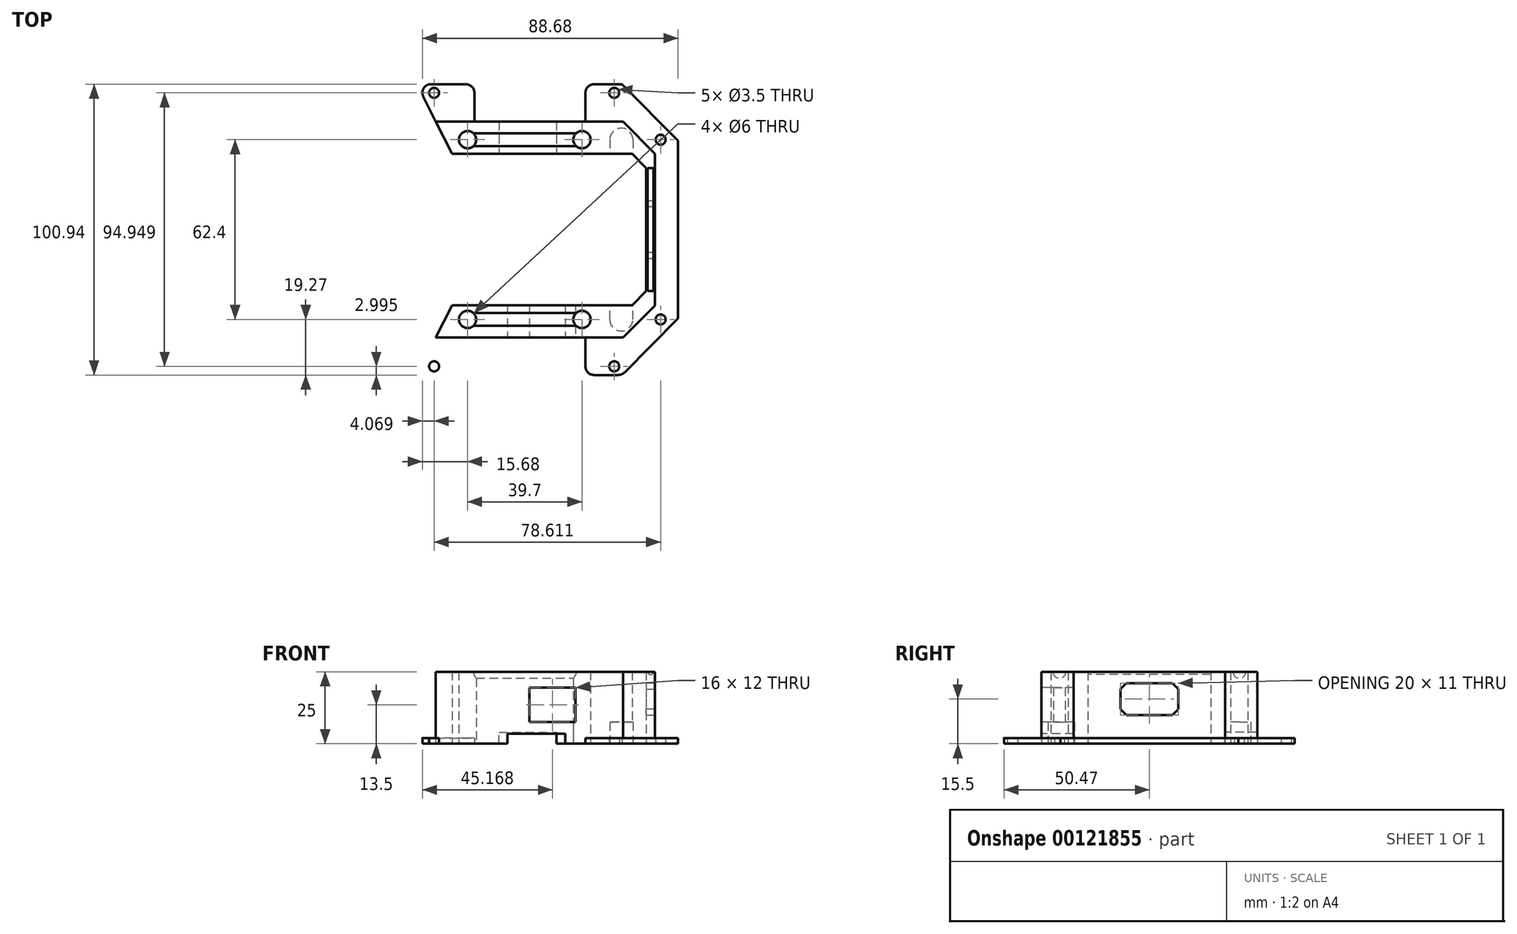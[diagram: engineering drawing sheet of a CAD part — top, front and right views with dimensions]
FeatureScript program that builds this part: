
annotation { "Feature Type Name" : "Feature", "Feature Type Description" : "" }
export const myFeature = defineFeature(function(context is Context, id is Id, definition is map)
    precondition{}
    {
        {
            var Q0;
            Q0=qCreatedBy(makeId("Top.planeOp"),FACE);
            var sketch = newSketch(context, id + "F0", { "sketchPlane" : qUnion([Q0])});
            skCircle(sketch, "E0", {"center": v(-9.61, 47.47) * mm, "radius": 1.75 * mm});
            skCircle(sketch, "E1", {"center": v(52.89, 47.47) * mm, "radius": 1.75 * mm});
            skCircle(sketch, "E2", {"center": v(69, 31.2) * mm, "radius": 1.75 * mm});
            skCircle(sketch, "E3", {"center": v(2, 31.2) * mm, "radius": 3 * mm});
            skLineSegment(sketch, "E4.MirrorCS", {"start": v(55.55, 50.47) * mm, "end": v(-15.54, 50.47) * mm});
            skLineSegment(sketch, "E5.MirrorCS", {"start": v(-9.01, 37.47) * mm, "end": v(55.99, 37.47) * mm});
            skCircle(sketch, "E6", {"center": v(41.7, 31.2) * mm, "radius": 3 * mm});
            skLineSegment(sketch, "E7", {"start": v(-5.97, 31.4) * mm, "end": v(-15.54, 50.47) * mm});
            skLineSegment(sketch, "E8", {"start": v(52.89, 47.47) * mm, "end": v(69, 31.2) * mm, "construction": true});
            skLineSegment(sketch, "E9", {"start": v(55.55, 50.47) * mm, "end": v(75, 30.82) * mm});
            skLineSegment(sketch, "E10", {"start": v(55.99, 37.47) * mm, "end": v(67, 26.35) * mm});
            skLineSegment(sketch, "E11", {"start": v(75, 30.82) * mm, "end": v(75, -30.82) * mm});
            skLineSegment(sketch, "E12", {"start": v(69, 31.2) * mm, "end": v(2, 31.2) * mm, "construction": true});
            skLineSegment(sketch, "E13", {"start": v(65.5, 40.42) * mm, "end": v(62.66, 37.6) * mm, "construction": true});
            skCircle(sketch, "E14.MirrorC", {"center": v(52.89, -47.47) * mm, "radius": 1.75 * mm});
            skCircle(sketch, "E15.MirrorC", {"center": v(69, -31.2) * mm, "radius": 1.75 * mm});
            skLineSegment(sketch, "E16.MirrorCS", {"start": v(62.66, -37.6) * mm, "end": v(58.9, -34.3) * mm, "construction": true});
            skCircle(sketch, "E17.MirrorC", {"center": v(-9.61, -47.47) * mm, "radius": 1.75 * mm});
            skLineSegment(sketch, "E18.MirrorCS", {"start": v(65.5, -40.42) * mm, "end": v(62.66, -37.6) * mm, "construction": true});
            skLineSegment(sketch, "E19.MirrorCS", {"start": v(55.99, -37.47) * mm, "end": v(67, -26.35) * mm});
            skLineSegment(sketch, "E20.MirrorCS", {"start": v(-5.97, -31.4) * mm, "end": v(-15.54, -50.47) * mm});
            skLineSegment(sketch, "E21.MirrorCS", {"start": v(52.89, -47.47) * mm, "end": v(-9.61, -47.47) * mm, "construction": true});
            skCircle(sketch, "E22.MirrorC", {"center": v(41.7, -31.2) * mm, "radius": 3 * mm});
            skLineSegment(sketch, "E23.MirrorCS", {"start": v(-9.01, -37.47) * mm, "end": v(55.99, -37.47) * mm});
            skCircle(sketch, "E24.MirrorC", {"center": v(2, -31.2) * mm, "radius": 3 * mm});
            skLineSegment(sketch, "E25.MirrorCS", {"start": v(55.55, -50.47) * mm, "end": v(75, -30.82) * mm});
            skLineSegment(sketch, "E26.MirrorCS", {"start": v(52.89, -47.47) * mm, "end": v(69, -31.2) * mm, "construction": true});
            skLineSegment(sketch, "E27.MirrorCS", {"start": v(69, -31.2) * mm, "end": v(2, -31.2) * mm, "construction": true});
            skLineSegment(sketch, "E28.MirrorCS", {"start": v(55.55, -50.47) * mm, "end": v(-15.54, -50.47) * mm});
            skLineSegment(sketch, "E29", {"start": v(67, 26.35) * mm, "end": v(67, -26.35) * mm});
            skLineSegment(sketch, "E30", {"start": v(-5.86, 31.2) * mm, "end": v(62.2, 31.2) * mm});
            skLineSegment(sketch, "E31.MirrorCS", {"start": v(-5.86, -31.2) * mm, "end": v(62.2, -31.2) * mm});
            skLineSegment(sketch, "E32", {"start": v(42.89, 50.47) * mm, "end": v(42.89, 37.47) * mm});
            skLineSegment(sketch, "E33", {"start": v(4.39, 50.47) * mm, "end": v(4.39, 37.47) * mm});
            skLineSegment(sketch, "E34.MirrorCS", {"start": v(42.89, -50.47) * mm, "end": v(42.89, -37.47) * mm});
            skLineSegment(sketch, "E35.MirrorCS", {"start": v(4.39, -50.47) * mm, "end": v(4.39, -37.47) * mm});
            skLineSegment(sketch, "E36", {"start": v(54.2, -31.2) * mm, "end": v(64, -21.3) * mm});
            skLineSegment(sketch, "E37.MirrorCS", {"start": v(54.2, 31.2) * mm, "end": v(64, 21.3) * mm});
            skLineSegment(sketch, "E38", {"start": v(64, 21.3) * mm, "end": v(64, -21.3) * mm});
            skLineSegment(sketch, "E39", {"start": v(59.1, 26.25) * mm, "end": v(-3.38, 26.25) * mm});
            skLineSegment(sketch, "E40", {"start": v(-3.38, 26.25) * mm, "end": v(-5.97, 31.4) * mm});
            skLineSegment(sketch, "E41.MirrorCS", {"start": v(59.1, -26.25) * mm, "end": v(-3.38, -26.25) * mm});
            skLineSegment(sketch, "E42.MirrorCS", {"start": v(-3.38, -26.25) * mm, "end": v(-5.97, -31.4) * mm});
            skLineSegment(sketch, "E43", {"start": v(52.89, 47.47) * mm, "end": v(-9.61, 47.47) * mm, "construction": true});
            skSolve(sketch);
        }
        {
            var Q0;
            {var subQ0=sQuery(id+"F0.wireOp",EDGE,"4sFYRNq8-8Jgj-4G77-OglM-QNHqH1h9Sw3j");Q0=makeQuery(id+"F0.imprint","IMPRINT",FACE,{"disambiguationData":[TD([[makeQuery(id+"F0.imprint","IMPRINT",EDGE,{"derivedFrom":subQ0}),-1.0]])]});}
            var Q1;
            {var subQ7=sQuery(id+"F0.wireOp",EDGE,"8FFk7yXp-FnWU-P27a-pTHK-MUgHDnBpdSHA");Q1=makeQuery(id+"F0.imprint","IMPRINT",FACE,{"disambiguationData":[TD([[makeQuery(id+"F0.imprint","IMPRINT",EDGE,{"derivedFrom":subQ7}),-1.0]])]});}
            var Q2;
            Q2=makeQuery(id+"F0.imprint","IMPRINT",FACE,{"disambiguationData":[TD([[makeQuery(id+"F0.imprint","IMPRINT",EDGE,{"derivedFrom":sQuery(id+"F0.wireOp",EDGE,"E0")}),-1.0]])]});
            var Q3;
            Q3=makeQuery(id+"F0.imprint","IMPRINT",FACE,{"disambiguationData":[TD([[makeQuery(id+"F0.imprint","IMPRINT",EDGE,{"derivedFrom":sQuery(id+"F0.wireOp",EDGE,"4ea4419b-eab7-4580-8047-e2baf9f9c4100.MirrorC")}),1.0]])]});
            var Q4;
            Q4=makeQuery(id+"F0.imprint","IMPRINT",FACE,{"disambiguationData":[TD([[makeQuery(id+"F0.imprint","IMPRINT",EDGE,{"derivedFrom":sQuery(id+"F0.wireOp",EDGE,"f24bded4-04d1-417a-8021-171b2d75794f0.MirrorC")}),1.0]])]});
            var Q5;
            {var subQ0=sQuery(id+"F0.wireOp",EDGE,"pAdb5JEh-NYMF-ctJB-lSUV-qMQ0hBkF58aF");var subQ1=sQuery(id+"F0.wireOp",EDGE,"931a9ce9-199b-493e-a000-b7f4cd656f313.MirrorCS");var subQ2=makeQuery(id+"F0.imprint","INTERSECT",VERTEX,{"derivedFrom":[subQ1,subQ0]});Q5=makeQuery(id+"F0.imprint","IMPRINT",FACE,{"disambiguationData":[TD([[makeQuery(id+"F0.imprint","IMPRINT",EDGE,{"disambiguationData":[TD([[subQ2,-1.0]])],"derivedFrom":subQ1}),-1.0]])]});}
            var Q6;
            Q6=makeQuery(id+"F0.imprint","IMPRINT",FACE,{"disambiguationData":[TD([[makeQuery(id+"F0.imprint","IMPRINT",EDGE,{"derivedFrom":sQuery(id+"F0.wireOp",EDGE,"f24bded4-04d1-417a-8021-171b2d75794f1.MirrorC")}),1.0]])]});
            var Q7;
            Q7=makeQuery(id+"F0.imprint","IMPRINT",FACE,{"disambiguationData":[TD([[makeQuery(id+"F0.imprint","IMPRINT",EDGE,{"derivedFrom":sQuery(id+"F0.wireOp",EDGE,"E1")}),-1.0]])]});
            var Q8;
            Q8=makeQuery(id+"F0.imprint","IMPRINT",FACE,{"disambiguationData":[TD([[makeQuery(id+"F0.imprint","IMPRINT",EDGE,{"derivedFrom":sQuery(id+"F0.wireOp",EDGE,"E17.MirrorC")}),1.0]])]});
            extrude(context, id + "F1", {"entities" : qUnion([Q0, Q1, Q2, Q3, Q4, Q5, Q6, Q7, Q8]), "depth" : 2 * mm, "offsetDistance" : 25 * mm});
        }
        {
            var Q0;
            {var subQ1=sQuery(id+"F0.wireOp",EDGE,"a8754a4c-98fa-47e2-aac1-e6e8d69fb4766.MirrorCS");var subQ3=sQuery(id+"F0.wireOp",EDGE,"a8754a4c-98fa-47e2-aac1-e6e8d69fb4767.MirrorCS");var subQ4=makeQuery(id+"F0.imprint","INTERSECT",VERTEX,{"derivedFrom":[subQ1,subQ3]});Q0=makeQuery(id+"F0.imprint","IMPRINT",FACE,{"disambiguationData":[TD([[makeQuery(id+"F0.imprint","IMPRINT",EDGE,{"disambiguationData":[TD([[subQ4,1.0]])],"derivedFrom":subQ3}),-1.0]])]});}
            var Q1;
            {var subQ7=sQuery(id+"F0.wireOp",EDGE,"a8754a4c-98fa-47e2-aac1-e6e8d69fb4764.MirrorCS");Q1=makeQuery(id+"F0.imprint","IMPRINT",FACE,{"disambiguationData":[TD([[makeQuery(id+"F0.imprint","IMPRINT",EDGE,{"derivedFrom":subQ7}),1.0]])]});}
            var Q2;
            {var subQ6=sQuery(id+"F0.wireOp",EDGE,"E5.MirrorCS");Q2=makeQuery(id+"F0.imprint","IMPRINT",FACE,{"disambiguationData":[TD([[makeQuery(id+"F0.imprint","IMPRINT",EDGE,{"derivedFrom":subQ6}),-1.0]])]});}
            var Q3;
            {var subQ1=sQuery(id+"F0.wireOp",EDGE,"dWmuS8xV-OHKk-HRkj-rr6b-XV2wZqhuztuN");Q3=makeQuery(id+"F0.imprint","IMPRINT",FACE,{"disambiguationData":[TD([[makeQuery(id+"F0.imprint","IMPRINT",EDGE,{"derivedFrom":subQ1}),1.0]])]});}
            var Q4;
            {var subQ8=sQuery(id+"F0.wireOp",EDGE,"4ea4419b-eab7-4580-8047-e2baf9f9c4108.MirrorCS");Q4=makeQuery(id+"F0.imprint","IMPRINT",FACE,{"disambiguationData":[TD([[makeQuery(id+"F0.imprint","IMPRINT",EDGE,{"derivedFrom":subQ8}),1.0]])]});}
            var Q5;
            {var subQ1=sQuery(id+"F0.wireOp",EDGE,"4ea4419b-eab7-4580-8047-e2baf9f9c4102.MirrorCS");var subQ3=sQuery(id+"F0.wireOp",EDGE,"4ea4419b-eab7-4580-8047-e2baf9f9c4103.MirrorCS");var subQ4=makeQuery(id+"F0.imprint","INTERSECT",VERTEX,{"derivedFrom":[subQ1,subQ3]});Q5=makeQuery(id+"F0.imprint","IMPRINT",FACE,{"disambiguationData":[TD([[makeQuery(id+"F0.imprint","IMPRINT",EDGE,{"disambiguationData":[TD([[subQ4,-1.0]])],"derivedFrom":subQ3}),-1.0]])]});}
            var Q6;
            {var subQ5=sQuery(id+"F0.wireOp",EDGE,"pAdb5JEh-NYMF-ctJB-lSUV-qMQ0hBkF58aF");Q6=makeQuery(id+"F0.imprint","IMPRINT",FACE,{"disambiguationData":[TD([[makeQuery(id+"F0.imprint","IMPRINT",EDGE,{"derivedFrom":subQ5}),-1.0]])]});}
            var Q7;
            {var subQ0=sQuery(id+"F0.wireOp",EDGE,"4ea4419b-eab7-4580-8047-e2baf9f9c4105.MirrorCS");var subQ1=sQuery(id+"F0.wireOp",EDGE,"4ea4419b-eab7-4580-8047-e2baf9f9c4103.MirrorCS");var subQ2=makeQuery(id+"F0.imprint","INTERSECT",VERTEX,{"derivedFrom":[subQ1,subQ0]});Q7=makeQuery(id+"F0.imprint","IMPRINT",FACE,{"disambiguationData":[TD([[makeQuery(id+"F0.imprint","IMPRINT",EDGE,{"disambiguationData":[TD([[subQ2,-1.0]])],"derivedFrom":subQ1}),-1.0]])]});}
            var Q8;
            {var subQ5=sQuery(id+"F0.wireOp",EDGE,"f24bded4-04d1-417a-8021-171b2d75794f8.MirrorCS");Q8=makeQuery(id+"F0.imprint","IMPRINT",FACE,{"disambiguationData":[TD([[makeQuery(id+"F0.imprint","IMPRINT",EDGE,{"derivedFrom":subQ5}),1.0]])]});}
            var Q9;
            {var subQ0=sQuery(id+"F0.wireOp",EDGE,"f24bded4-04d1-417a-8021-171b2d75794f7.MirrorCS");Q9=makeQuery(id+"F0.imprint","IMPRINT",FACE,{"disambiguationData":[TD([[makeQuery(id+"F0.imprint","IMPRINT",EDGE,{"derivedFrom":subQ0}),1.0]])]});}
            var Q10;
            {var subQ5=sQuery(id+"F0.wireOp",EDGE,"a31a7e4d-a42e-4eae-b5b2-72da23cc9b960.MirrorCS");Q10=makeQuery(id+"F0.imprint","IMPRINT",FACE,{"disambiguationData":[TD([[makeQuery(id+"F0.imprint","IMPRINT",EDGE,{"derivedFrom":subQ5}),-1.0]])]});}
            var Q11;
            {var subQ4=sQuery(id+"F0.wireOp",EDGE,"4ea4419b-eab7-4580-8047-e2baf9f9c41013.MirrorCS");var subQ6=sQuery(id+"F0.wireOp",EDGE,"pAdb5JEh-NYMF-ctJB-lSUV-qMQ0hBkF58aF");var subQ7=makeQuery(id+"F0.imprint","INTERSECT",VERTEX,{"derivedFrom":[subQ6,subQ4]});Q11=makeQuery(id+"F0.imprint","IMPRINT",FACE,{"disambiguationData":[TD([[makeQuery(id+"F0.imprint","IMPRINT",EDGE,{"disambiguationData":[TD([[subQ7,1.0]])],"derivedFrom":subQ6}),-1.0]])]});}
            var Q12;
            {var subQ0=sQuery(id+"F0.wireOp",EDGE,"E23.MirrorCS");var subQ9=sQuery(id+"F0.wireOp",EDGE,"E19.MirrorCS");var subQ10=makeQuery(id+"F0.imprint","INTERSECT",VERTEX,{"derivedFrom":[subQ9,subQ0]});Q12=makeQuery(id+"F0.imprint","IMPRINT",FACE,{"disambiguationData":[TD([[makeQuery(id+"F0.imprint","IMPRINT",EDGE,{"disambiguationData":[TD([[subQ10,-1.0]])],"derivedFrom":subQ9}),1.0]])]});}
            var Q13;
            {var subQ4=sQuery(id+"F0.wireOp",EDGE,"E29");Q13=makeQuery(id+"F0.imprint","IMPRINT",FACE,{"disambiguationData":[TD([[makeQuery(id+"F0.imprint","IMPRINT",EDGE,{"derivedFrom":subQ4}),-1.0]])]});}
            var Q14;
            {var subQ10=sQuery(id+"F0.wireOp",EDGE,"E39");Q14=makeQuery(id+"F0.imprint","IMPRINT",FACE,{"disambiguationData":[TD([[makeQuery(id+"F0.imprint","IMPRINT",EDGE,{"derivedFrom":subQ10}),-1.0]])]});}
            var Q15;
            {var subQ9=sQuery(id+"F0.wireOp",EDGE,"E41.MirrorCS");Q15=makeQuery(id+"F0.imprint","IMPRINT",FACE,{"disambiguationData":[TD([[makeQuery(id+"F0.imprint","IMPRINT",EDGE,{"derivedFrom":subQ9}),1.0]])]});}
            extrude(context, id + "F2", {"entities" : qUnion([Q0, Q1, Q2, Q3, Q4, Q5, Q6, Q7, Q8, Q9, Q10, Q11, Q12, Q13, Q14, Q15]), "operationType" : NewBodyOperationType.ADD, "depth" : 25 * mm, "offsetDistance" : 25 * mm});
        }
        {
            var Q0;
            Q0=makeQuery(id+"F2.opExtrude","SWEPT_FACE",FACE,{"disambiguationData":[OSD([sQuery(id+"F0.wireOp",EDGE,"E29")])]});
            var sketch = newSketch(context, id + "F3", { "sketchPlane" : qUnion([Q0])});
            skLineSegment(sketch, "E44.bottom", {"start": v(-10, 21) * mm, "end": v(10, 21) * mm});
            skLineSegment(sketch, "E44.top", {"start": v(-10, 10) * mm, "end": v(10, 10) * mm});
            skLineSegment(sketch, "E44.left", {"start": v(-10, 21) * mm, "end": v(-10, 10) * mm});
            skLineSegment(sketch, "E44.right", {"start": v(10, 21) * mm, "end": v(10, 10) * mm});
            skLineSegment(sketch, "E45", {"start": v(0, 25) * mm, "end": v(0, 0) * mm});
            skSolve(sketch);
        }
        {
            var Q0;
            Q0 = qSketchRegion(id + "F3", true);
            extrude(context, id + "F4", {"entities" : qUnion([Q0]), "operationType" : NewBodyOperationType.REMOVE, "endBound" : BoundingType.SYMMETRIC, "oppositeDirection" : true, "depth" : 25 * mm, "offsetDistance" : 25 * mm});
        }
        {
            var Q0;
            Q0=makeQuery(id+"F2.opExtrude","SWEPT_FACE",FACE,{"disambiguationData":[OSD([sQuery(id+"F0.wireOp",EDGE,"E23.MirrorCS")])]});
            var sketch = newSketch(context, id + "F5", { "sketchPlane" : qUnion([Q0])});
            skLineSegment(sketch, "E46.bottom", {"start": v(23.49, 19.5) * mm, "end": v(39.49, 19.5) * mm});
            skLineSegment(sketch, "E46.top", {"start": v(23.49, 7.5) * mm, "end": v(39.49, 7.5) * mm});
            skLineSegment(sketch, "E46.left", {"start": v(23.49, 19.5) * mm, "end": v(23.49, 7.5) * mm});
            skLineSegment(sketch, "E46.right", {"start": v(39.49, 19.5) * mm, "end": v(39.49, 7.5) * mm});
            skLineSegment(sketch, "E47.bottom", {"start": v(93.3, 292.9) * mm, "end": v(83.7, 292.9) * mm});
            skLineSegment(sketch, "E47.top", {"start": v(93.3, 243.57) * mm, "end": v(83.7, 243.57) * mm});
            skLineSegment(sketch, "E47.left", {"start": v(93.3, 292.9) * mm, "end": v(93.3, 243.57) * mm});
            skLineSegment(sketch, "E47.right", {"start": v(83.7, 292.9) * mm, "end": v(83.7, 243.57) * mm});
            skLineSegment(sketch, "E48", {"start": v(15.89, 0) * mm, "end": v(15.89, 3.5) * mm});
            skLineSegment(sketch, "E49", {"start": v(15.89, 3.5) * mm, "end": v(35.89, 3.5) * mm});
            skLineSegment(sketch, "E50", {"start": v(35.89, 3.5) * mm, "end": v(35.89, 0) * mm});
            skLineSegment(sketch, "E51", {"start": v(35.89, 0) * mm, "end": v(15.89, 0) * mm});
            skSolve(sketch);
        }
        {
            var Q0;
            Q0=makeQuery(id+"F2.opExtrude","SWEPT_FACE",FACE,{"disambiguationData":[OSD([sQuery(id+"F0.wireOp",EDGE,"E5.MirrorCS")])]});
            var sketch = newSketch(context, id + "F6", { "sketchPlane" : qUnion([Q0])});
            skLineSegment(sketch, "E52", {"start": v(-32.89, 0) * mm, "end": v(-32.89, 4) * mm});
            skLineSegment(sketch, "E53", {"start": v(-32.89, 4) * mm, "end": v(-12.89, 4) * mm});
            skLineSegment(sketch, "E54", {"start": v(-12.89, 4) * mm, "end": v(-12.89, 0) * mm});
            skLineSegment(sketch, "E55", {"start": v(-12.89, 0) * mm, "end": v(-32.89, 0) * mm});
            skSolve(sketch);
        }
        {
            var Q0;
            Q0 = qSketchRegion(id + "F5", true);
            var Q1;
            Q1=makeQuery(id+"F6.imprint","IMPRINT",FACE,{"disambiguationData":[TD([[makeQuery(id+"F6.imprint","IMPRINT",EDGE,{"derivedFrom":sQuery(id+"F6.wireOp",EDGE,"E52")}),-1.0]])]});
            extrude(context, id + "F7", {"entities" : qUnion([Q0, Q1]), "operationType" : NewBodyOperationType.REMOVE, "endBound" : BoundingType.SYMMETRIC, "oppositeDirection" : true, "depth" : 25 * mm, "offsetDistance" : 25 * mm});
        }
        {
            var Q0;
            {var subQ0=sQuery(id+"F0.wireOp",EDGE,"E5.MirrorCS");Q0=makeQuery(id+"F1.opExtrude","CAP_EDGE",EDGE,{"disambiguationData":[OSD([subQ0]),TDD([makeQuery(id+"F0.imprint","IMPRINT",EDGE,{"disambiguationData":[TD([[makeQuery(id+"F0.imprint","INTERSECT",VERTEX,{"derivedFrom":[subQ0,sQuery(id+"F0.wireOp",EDGE,"E10")]}),1.0]])],"derivedFrom":subQ0})])],"isStart":false});}
            var Q1;
            {var subQ0=sQuery(id+"F0.wireOp",EDGE,"E5.MirrorCS");Q1=makeQuery(id+"F1.opExtrude","CAP_EDGE",EDGE,{"disambiguationData":[OSD([subQ0]),TDD([makeQuery(id+"F0.imprint","IMPRINT",EDGE,{"disambiguationData":[TD([[makeQuery(id+"F0.imprint","INTERSECT",VERTEX,{"derivedFrom":[subQ0,sQuery(id+"F0.wireOp",EDGE,"E7")]}),-1.0]])],"derivedFrom":subQ0})])],"isStart":false});}
            var Q2;
            Q2=makeQuery(id+"F1.opExtrude","CAP_EDGE",EDGE,{"disambiguationData":[OSD([sQuery(id+"F0.wireOp",EDGE,"E10")])],"isStart":false});
            var Q3;
            Q3=makeQuery(id+"F1.opExtrude","CAP_EDGE",EDGE,{"disambiguationData":[OSD([sQuery(id+"F0.wireOp",EDGE,"E29")])],"isStart":false});
            var Q4;
            Q4=makeQuery(id+"F1.opExtrude","CAP_EDGE",EDGE,{"disambiguationData":[OSD([sQuery(id+"F0.wireOp",EDGE,"E19.MirrorCS")])],"isStart":false});
            var Q5;
            {var subQ0=sQuery(id+"F0.wireOp",EDGE,"E23.MirrorCS");Q5=makeQuery(id+"F1.opExtrude","CAP_EDGE",EDGE,{"disambiguationData":[OSD([subQ0]),TDD([makeQuery(id+"F0.imprint","IMPRINT",EDGE,{"disambiguationData":[TD([[makeQuery(id+"F0.imprint","INTERSECT",VERTEX,{"derivedFrom":[sQuery(id+"F0.wireOp",EDGE,"E19.MirrorCS"),subQ0]}),1.0]])],"derivedFrom":subQ0})])],"isStart":false});}
            var Q6;
            {var subQ0=sQuery(id+"F0.wireOp",EDGE,"E23.MirrorCS");Q6=makeQuery(id+"F1.opExtrude","CAP_EDGE",EDGE,{"disambiguationData":[OSD([subQ0]),TDD([makeQuery(id+"F0.imprint","IMPRINT",EDGE,{"disambiguationData":[TD([[makeQuery(id+"F0.imprint","INTERSECT",VERTEX,{"derivedFrom":[sQuery(id+"F0.wireOp",EDGE,"E20.MirrorCS"),subQ0]}),-1.0]])],"derivedFrom":subQ0})])],"isStart":false});}
            var Q7;
            Q7=makeQuery(id+"F1.opExtrude","SWEPT_EDGE",EDGE,{"disambiguationData":[OSD([sQuery(id+"F0.wireOp",EDGE,"E5.MirrorCS"),sQuery(id+"F0.wireOp",EDGE,"E33")])]});
            var Q8;
            Q8=makeQuery(id+"F1.opExtrude","SWEPT_EDGE",EDGE,{"disambiguationData":[OSD([sQuery(id+"F0.wireOp",EDGE,"E5.MirrorCS"),sQuery(id+"F0.wireOp",EDGE,"E32")])]});
            var Q9;
            Q9=makeQuery(id+"F1.opExtrude","SWEPT_EDGE",EDGE,{"disambiguationData":[OSD([sQuery(id+"F0.wireOp",EDGE,"E23.MirrorCS"),sQuery(id+"F0.wireOp",EDGE,"E35.MirrorCS")])]});
            var Q10;
            Q10=makeQuery(id+"F1.opExtrude","SWEPT_EDGE",EDGE,{"disambiguationData":[OSD([sQuery(id+"F0.wireOp",EDGE,"E23.MirrorCS"),sQuery(id+"F0.wireOp",EDGE,"E34.MirrorCS")])]});
            var Q11;
            Q11=makeQuery(id+"F1.opExtrude","SWEPT_EDGE",EDGE,{"disambiguationData":[OSD([sQuery(id+"F0.wireOp",EDGE,"E4.MirrorCS"),sQuery(id+"F0.wireOp",EDGE,"E7")])]});
            var Q12;
            Q12=makeQuery(id+"F1.opExtrude","SWEPT_EDGE",EDGE,{"disambiguationData":[OSD([sQuery(id+"F0.wireOp",EDGE,"E20.MirrorCS"),sQuery(id+"F0.wireOp",EDGE,"E28.MirrorCS")])]});
            var Q13;
            Q13=makeQuery(id+"F1.opExtrude","SWEPT_EDGE",EDGE,{"disambiguationData":[OSD([sQuery(id+"F0.wireOp",EDGE,"E4.MirrorCS"),sQuery(id+"F0.wireOp",EDGE,"E32")])]});
            var Q14;
            Q14=makeQuery(id+"F1.opExtrude","SWEPT_EDGE",EDGE,{"disambiguationData":[OSD([sQuery(id+"F0.wireOp",EDGE,"E4.MirrorCS"),sQuery(id+"F0.wireOp",EDGE,"E33")])]});
            var Q15;
            Q15=makeQuery(id+"F1.opExtrude","SWEPT_EDGE",EDGE,{"disambiguationData":[OSD([sQuery(id+"F0.wireOp",EDGE,"E28.MirrorCS"),sQuery(id+"F0.wireOp",EDGE,"E34.MirrorCS")])]});
            var Q16;
            Q16=makeQuery(id+"F1.opExtrude","SWEPT_EDGE",EDGE,{"disambiguationData":[OSD([sQuery(id+"F0.wireOp",EDGE,"E28.MirrorCS"),sQuery(id+"F0.wireOp",EDGE,"E35.MirrorCS")])]});
            fillet(context, id + "F8", {"entities" : qUnion([Q0, Q1, Q2, Q3, Q4, Q5, Q6, Q7, Q8, Q9, Q10, Q11, Q12, Q13, Q14, Q15, Q16]), "radius" : 3 * mm, "tangentPropagation" : true, "allowEdgeOverflow" : false});
        }
        {
            var Q0;
            {var subQ0=sQuery(id+"F0.wireOp",EDGE,"E29");var subQ1=sQuery(id+"F0.wireOp",EDGE,"E23.MirrorCS");var subQ2=sQuery(id+"F0.wireOp",EDGE,"E20.MirrorCS");var subQ3=sQuery(id+"F0.wireOp",EDGE,"E19.MirrorCS");var subQ4=sQuery(id+"F0.wireOp",EDGE,"E10");var subQ5=sQuery(id+"F0.wireOp",EDGE,"E7");var subQ6=sQuery(id+"F0.wireOp",EDGE,"E5.MirrorCS");var subQ7=sQuery(id+"F0.wireOp",EDGE,"E28.MirrorCS");var subQ8=sQuery(id+"F0.wireOp",EDGE,"E4.MirrorCS");Q0=makeQuery(id+"F2.boolean.opBoolean","MERGE",FACE,{"derivedFrom":[makeQuery(id+"F1.opExtrude","CAP_FACE",FACE,{"disambiguationData":[OSD([sQuery(id+"F0.wireOp",EDGE,"E0"),subQ8,subQ6,subQ5,sQuery(id+"F0.wireOp",EDGE,"E33")])],"isStart":true}),makeQuery(id+"F1.opExtrude","CAP_FACE",FACE,{"disambiguationData":[OSD([sQuery(id+"F0.wireOp",EDGE,"E1"),sQuery(id+"F0.wireOp",EDGE,"E2"),subQ8,subQ6,sQuery(id+"F0.wireOp",EDGE,"E9"),subQ4,sQuery(id+"F0.wireOp",EDGE,"E11"),sQuery(id+"F0.wireOp",EDGE,"E14.MirrorC"),sQuery(id+"F0.wireOp",EDGE,"E15.MirrorC"),subQ3,subQ1,sQuery(id+"F0.wireOp",EDGE,"E25.MirrorCS"),subQ7,subQ0,sQuery(id+"F0.wireOp",EDGE,"E32"),sQuery(id+"F0.wireOp",EDGE,"E34.MirrorCS")])],"isStart":true}),makeQuery(id+"F1.opExtrude","CAP_FACE",FACE,{"disambiguationData":[OSD([sQuery(id+"F0.wireOp",EDGE,"E17.MirrorC"),subQ2,subQ1,subQ7,sQuery(id+"F0.wireOp",EDGE,"E35.MirrorCS")])],"isStart":true}),makeQuery(id+"F2.opExtrude","CAP_FACE",FACE,{"disambiguationData":[OSD([sQuery(id+"F0.wireOp",EDGE,"E3"),subQ6,sQuery(id+"F0.wireOp",EDGE,"E6"),subQ5,subQ4,subQ3,subQ2,sQuery(id+"F0.wireOp",EDGE,"E22.MirrorC"),subQ1,sQuery(id+"F0.wireOp",EDGE,"E24.MirrorC"),subQ0,sQuery(id+"F0.wireOp",EDGE,"E36"),sQuery(id+"F0.wireOp",EDGE,"E37.MirrorCS"),sQuery(id+"F0.wireOp",EDGE,"E38"),sQuery(id+"F0.wireOp",EDGE,"E39"),sQuery(id+"F0.wireOp",EDGE,"E40"),sQuery(id+"F0.wireOp",EDGE,"E41.MirrorCS"),sQuery(id+"F0.wireOp",EDGE,"E42.MirrorCS")])],"isStart":true})]});}
            var sketch = newSketch(context, id + "F9", { "sketchPlane" : qUnion([Q0])});
            skCircle(sketch, "E56", {"center": v(55.35, 31.2) * mm, "radius": 4 * mm});
            skCircle(sketch, "E57.MirrorC", {"center": v(55.35, -31.2) * mm, "radius": 4 * mm});
            skLineSegment(sketch, "E58", {"start": v(69, 31.2) * mm, "end": v(41.7, 31.2) * mm, "construction": true});
            skLineSegment(sketch, "E59", {"start": v(59.35, 31.2) * mm, "end": v(59.35, 26.25) * mm});
            skLineSegment(sketch, "E60", {"start": v(51.35, 31.2) * mm, "end": v(51.35, 26.25) * mm});
            skLineSegment(sketch, "E61", {"start": v(51.35, 26.25) * mm, "end": v(59.35, 26.25) * mm});
            skLineSegment(sketch, "E62.MirrorCS", {"start": v(59.35, -31.2) * mm, "end": v(59.35, -26.25) * mm});
            skLineSegment(sketch, "E63.MirrorCS", {"start": v(51.35, -31.2) * mm, "end": v(51.35, -26.25) * mm});
            skLineSegment(sketch, "E64.MirrorCS", {"start": v(69, -31.2) * mm, "end": v(41.7, -31.2) * mm, "construction": true});
            skLineSegment(sketch, "E65.MirrorCS", {"start": v(51.35, -26.25) * mm, "end": v(59.35, -26.25) * mm});
            skLineSegment(sketch, "E66", {"start": v(59.35, -26.25) * mm, "end": v(59.35, -26) * mm});
            skLineSegment(sketch, "E67", {"start": v(59.35, -26) * mm, "end": v(59.1, -26.25) * mm});
            skLineSegment(sketch, "E68.MirrorCS", {"start": v(59.35, 26) * mm, "end": v(59.1, 26.25) * mm});
            skLineSegment(sketch, "E69.MirrorCS", {"start": v(59.35, 26.25) * mm, "end": v(59.35, 26) * mm});
            skSolve(sketch);
        }
        {
            var Q0;
            Q0 = qSketchRegion(id + "F9", true);
            extrude(context, id + "F10", {"entities" : qUnion([Q0]), "operationType" : NewBodyOperationType.REMOVE, "oppositeDirection" : true, "depth" : 7.5 * mm, "offsetDistance" : 25 * mm});
        }
        {
            var Q0;
            Q0=makeQuery(id+"F2.opExtrude","CAP_FACE",FACE,{"disambiguationData":[OSD([sQuery(id+"F0.wireOp",EDGE,"E3"),sQuery(id+"F0.wireOp",EDGE,"E5.MirrorCS"),sQuery(id+"F0.wireOp",EDGE,"E6"),sQuery(id+"F0.wireOp",EDGE,"E7"),sQuery(id+"F0.wireOp",EDGE,"E10"),sQuery(id+"F0.wireOp",EDGE,"E19.MirrorCS"),sQuery(id+"F0.wireOp",EDGE,"E20.MirrorCS"),sQuery(id+"F0.wireOp",EDGE,"E22.MirrorC"),sQuery(id+"F0.wireOp",EDGE,"E23.MirrorCS"),sQuery(id+"F0.wireOp",EDGE,"E24.MirrorC"),sQuery(id+"F0.wireOp",EDGE,"E29"),sQuery(id+"F0.wireOp",EDGE,"E36"),sQuery(id+"F0.wireOp",EDGE,"E37.MirrorCS"),sQuery(id+"F0.wireOp",EDGE,"E38"),sQuery(id+"F0.wireOp",EDGE,"E39"),sQuery(id+"F0.wireOp",EDGE,"E40"),sQuery(id+"F0.wireOp",EDGE,"E41.MirrorCS"),sQuery(id+"F0.wireOp",EDGE,"E42.MirrorCS")])],"isStart":false});
            var sketch = newSketch(context, id + "F11", { "sketchPlane" : qUnion([Q0])});
            skLineSegment(sketch, "E70", {"start": v(2, 31.2) * mm, "end": v(41.7, 31.2) * mm});
            skLineSegment(sketch, "E71", {"start": v(65.5, 21.3) * mm, "end": v(65.5, -21.3) * mm});
            skLineSegment(sketch, "E72", {"start": v(65.5, 7.85) * mm, "end": v(64, 7.85) * mm, "construction": true});
            skLineSegment(sketch, "E73", {"start": v(65.5, 7.85) * mm, "end": v(67, 7.85) * mm, "construction": true});
            skLineSegment(sketch, "E74", {"start": v(64, 21.3) * mm, "end": v(67, 21.3) * mm, "construction": true});
            skLineSegment(sketch, "E75", {"start": v(64, -21.3) * mm, "end": v(67, -21.3) * mm, "construction": true});
            skLineSegment(sketch, "E76", {"start": v(41.7, 31.2) * mm, "end": v(41.7, 28.95) * mm});
            skLineSegment(sketch, "E77", {"start": v(41.7, 28.95) * mm, "end": v(2, 28.95) * mm});
            skLineSegment(sketch, "E78", {"start": v(2, 28.95) * mm, "end": v(2, 31.2) * mm});
            skLineSegment(sketch, "E79.MirrorCS", {"start": v(41.7, -31.2) * mm, "end": v(41.7, -28.95) * mm});
            skLineSegment(sketch, "E80.MirrorCS", {"start": v(2, -28.95) * mm, "end": v(2, -31.2) * mm});
            skLineSegment(sketch, "E81.MirrorCS", {"start": v(2, -31.2) * mm, "end": v(41.7, -31.2) * mm});
            skLineSegment(sketch, "E82.MirrorCS", {"start": v(41.7, -28.95) * mm, "end": v(2, -28.95) * mm});
            skLineSegment(sketch, "E83", {"start": v(66.5, 21.3) * mm, "end": v(66.5, -21.3) * mm});
            skLineSegment(sketch, "E84", {"start": v(66.5, -21.3) * mm, "end": v(65.5, -21.3) * mm});
            skLineSegment(sketch, "E85", {"start": v(66.5, 21.3) * mm, "end": v(65.5, 21.3) * mm});
            skLineSegment(sketch, "E86.MirrorCS", {"start": v(41.7, 31.2) * mm, "end": v(41.7, 33.45) * mm});
            skLineSegment(sketch, "E87.MirrorCS", {"start": v(41.7, 33.45) * mm, "end": v(2, 33.45) * mm});
            skLineSegment(sketch, "E88.MirrorCS", {"start": v(2, 33.45) * mm, "end": v(2, 31.2) * mm});
            skLineSegment(sketch, "E89.MirrorCS", {"start": v(41.7, -31.2) * mm, "end": v(41.7, -33.45) * mm});
            skLineSegment(sketch, "E90.MirrorCS", {"start": v(41.7, -33.45) * mm, "end": v(2, -33.45) * mm});
            skSolve(sketch);
        }
        {
            var Q0;
            Q0=makeQuery(id+"F11.imprint","IMPRINT",FACE,{"disambiguationData":[TD([[makeQuery(id+"F11.imprint","IMPRINT",EDGE,{"derivedFrom":sQuery(id+"F11.wireOp",EDGE,"E71")}),1.0]])]});
            var Q1;
            Q1=sQuery(id+"F11.wireOp",EDGE,"E71");
            revolve(context, id + "F12", {"operationType" : NewBodyOperationType.REMOVE, "surfaceOperationType" : NewSurfaceOperationType.NEW, "entities" : qUnion([Q0]), "axis" : qUnion([Q1]), "revolveType" : RevolveType.FULL, "oppositeDirection" : true});
        }
        {
            var Q0;
            {var subQ0=sQuery(id+"F11.wireOp",EDGE,"E70");var subQ1=makeQuery(id+"F2.opExtrude","CAP_EDGE",EDGE,{"disambiguationData":[OSD([sQuery(id+"F0.wireOp",EDGE,"E3")])],"isStart":false});var subQ2=makeQuery(id+"F11.imprint","INTERSECT",VERTEX,{"derivedFrom":[subQ1,subQ0]});Q0=makeQuery(id+"F11.imprint","IMPRINT",FACE,{"disambiguationData":[TD([[makeQuery(id+"F11.imprint","IMPRINT",EDGE,{"disambiguationData":[TD([[subQ2,-1.0]])],"derivedFrom":subQ0}),1.0]])]});}
            var Q1;
            Q1=sQuery(id+"F11.wireOp",EDGE,"E70");
            revolve(context, id + "F13", {"operationType" : NewBodyOperationType.REMOVE, "surfaceOperationType" : NewSurfaceOperationType.NEW, "entities" : qUnion([Q0]), "axis" : qUnion([Q1]), "revolveType" : RevolveType.FULL, "oppositeDirection" : true});
        }
        {
            var Q0;
            {var subQ0=sQuery(id+"F11.wireOp",EDGE,"E81.MirrorCS");var subQ1=makeQuery(id+"F2.opExtrude","CAP_EDGE",EDGE,{"disambiguationData":[OSD([sQuery(id+"F0.wireOp",EDGE,"E24.MirrorC")])],"isStart":false});var subQ2=makeQuery(id+"F11.imprint","INTERSECT",VERTEX,{"derivedFrom":[subQ1,subQ0]});Q0=makeQuery(id+"F11.imprint","IMPRINT",FACE,{"disambiguationData":[TD([[makeQuery(id+"F11.imprint","IMPRINT",EDGE,{"disambiguationData":[TD([[subQ2,-1.0]])],"derivedFrom":subQ0}),1.0]])]});}
            var Q1;
            Q1=sQuery(id+"F11.wireOp",EDGE,"E81.MirrorCS");
            revolve(context, id + "F14", {"operationType" : NewBodyOperationType.REMOVE, "surfaceOperationType" : NewSurfaceOperationType.NEW, "entities" : qUnion([Q0]), "axis" : qUnion([Q1]), "revolveType" : RevolveType.FULL, "oppositeDirection" : true});
        }
        {
            var Q0;
            Q0=makeQuery(id+"F4.boolean.opBoolean","COPY",EDGE,{"derivedFrom":makeQuery(id+"F4.opExtrude","SWEPT_EDGE",EDGE,{"disambiguationData":[OSD([sQuery(id+"F3.wireOp",EDGE,"E44.bottom"),sQuery(id+"F3.wireOp",EDGE,"E44.left")])]})});
            var Q1;
            Q1=makeQuery(id+"F4.boolean.opBoolean","COPY",EDGE,{"derivedFrom":makeQuery(id+"F4.opExtrude","SWEPT_EDGE",EDGE,{"disambiguationData":[OSD([sQuery(id+"F3.wireOp",EDGE,"E44.bottom"),sQuery(id+"F3.wireOp",EDGE,"E44.right")])]})});
            var Q2;
            Q2=makeQuery(id+"F4.boolean.opBoolean","COPY",EDGE,{"derivedFrom":makeQuery(id+"F4.opExtrude","SWEPT_EDGE",EDGE,{"disambiguationData":[OSD([sQuery(id+"F3.wireOp",EDGE,"E44.top"),sQuery(id+"F3.wireOp",EDGE,"E44.left")])]})});
            var Q3;
            Q3=makeQuery(id+"F4.boolean.opBoolean","COPY",EDGE,{"derivedFrom":makeQuery(id+"F4.opExtrude","SWEPT_EDGE",EDGE,{"disambiguationData":[OSD([sQuery(id+"F3.wireOp",EDGE,"E44.top"),sQuery(id+"F3.wireOp",EDGE,"E44.right")])]})});
            chamfer(context, id + "F15", {"entities" : qUnion([Q0, Q1, Q2, Q3]), "width" : 2 * mm, "tangentPropagation" : true});
        }
    });
